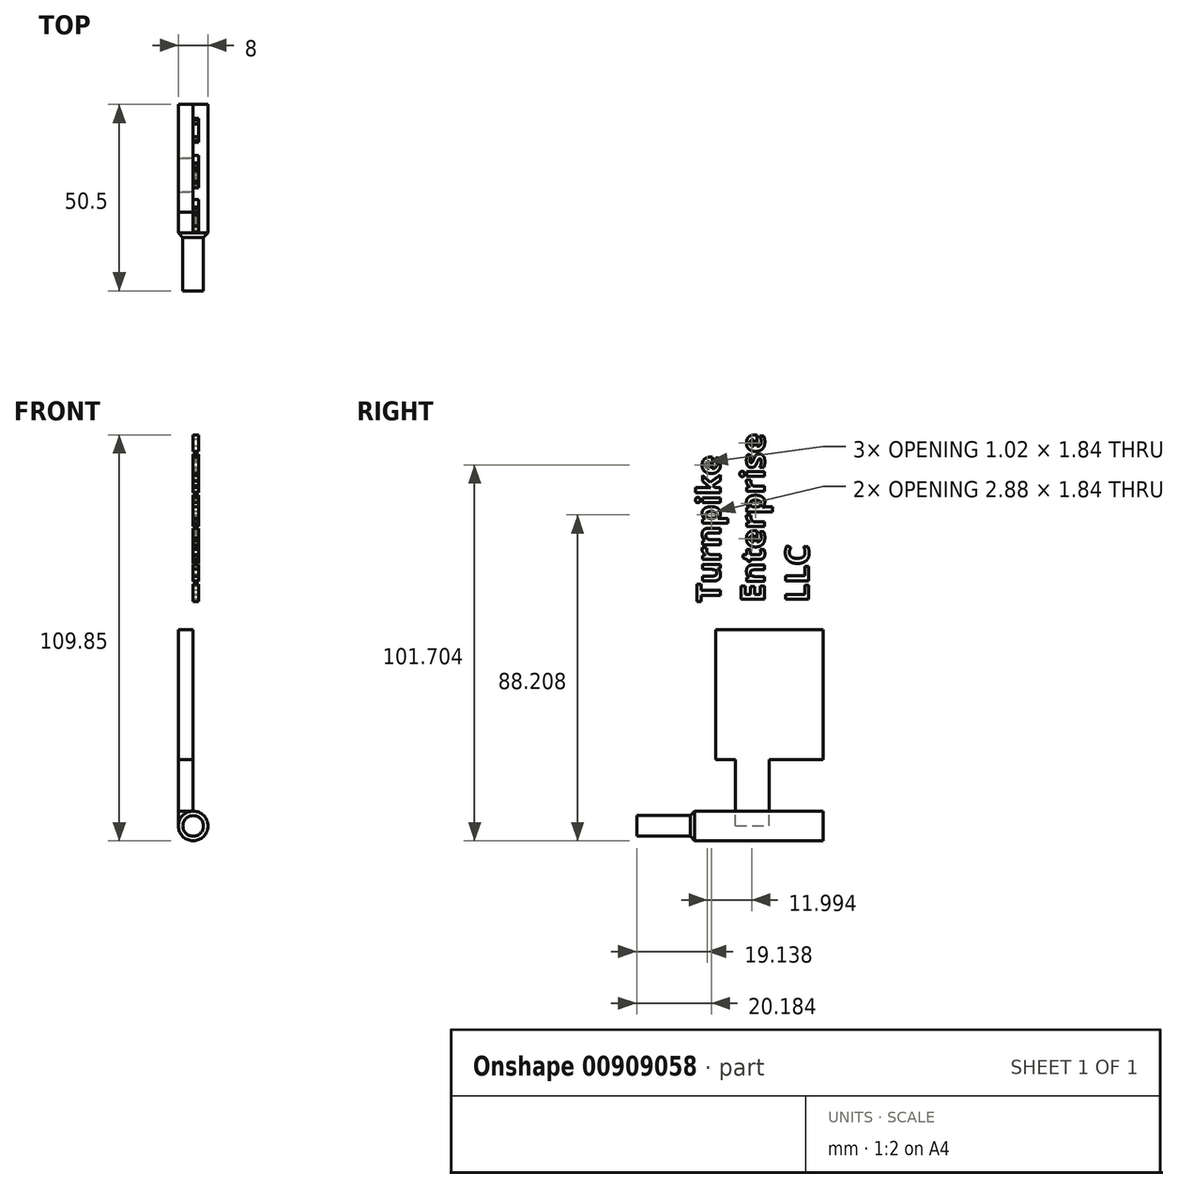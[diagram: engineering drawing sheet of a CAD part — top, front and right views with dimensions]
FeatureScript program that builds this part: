
annotation { "Feature Type Name" : "Feature", "Feature Type Description" : "" }
export const myFeature = defineFeature(function(context is Context, id is Id, definition is map)
    precondition{}
    {
        {
            var Q0;
            Q0=qCreatedBy(makeId("Right.planeOp"),FACE);
            cPlane(context, id + "F0", {"entities" : qUnion([Q0]), "cplaneType" : CPlaneType.OFFSET, "offset" : 4 * mm, "oppositeDirection" : true, "width" : 150 * mm, "height" : 150 * mm});
        }
        {
            var Q0;
            Q0=qCreatedBy(makeId("Front.planeOp"),FACE);
            var sketch = newSketch(context, id + "F1", { "sketchPlane" : qUnion([Q0])});
            skCircle(sketch, "E0", {"center": v(0, 0) * mm, "radius": 4 * mm});
            skSolve(sketch);
        }
        {
            var Q0;
            Q0=makeQuery(id+"F1.imprint","IMPRINT",FACE,{"disambiguationData":[TD([[makeQuery(id+"F1.imprint","IMPRINT",EDGE,{"derivedFrom":sQuery(id+"F1.wireOp",EDGE,"E0")}),1.0]])]});
            extrude(context, id + "F2", {"entities" : qUnion([Q0]), "endBound" : BoundingType.SYMMETRIC, "depth" : 21 * mm, "offsetDistance" : 25 * mm});
        }
        {
            var Q0;
            Q0=qCreatedBy(makeId("Front.planeOp"),FACE);
            var sketch = newSketch(context, id + "F3", { "sketchPlane" : qUnion([Q0])});
            skCircle(sketch, "E1", {"center": v(0, 0) * mm, "radius": 2.8 * mm});
            skSolve(sketch);
        }
        {
            var Q0;
            Q0 = qSketchRegion(id + "F3", true);
            extrude(context, id + "F4", {"entities" : qUnion([Q0]), "depth" : 40 * mm, "offsetDistance" : 25 * mm});
        }
        {
            var Q0;
            Q0=makeQuery(id+"F2.opExtrude","SWEPT_BODY",BODY,{"disambiguationData":[OSD([sQuery(id+"F1.wireOp",EDGE,"E0")])]});
            var Q1;
            Q1=makeQuery(id+"F4.opExtrude","SWEPT_BODY",BODY,{"disambiguationData":[OSD([sQuery(id+"F3.wireOp",EDGE,"E1")])]});
            booleanBodies(context, id + "F5", {"operationType" : BooleanOperationType.UNION, "tools" : qUnion([Q0, Q1])});
        }
        {
            var Q0;
            Q0=makeQuery(id+"F5.opBoolean","INTERSECT",EDGE,{"derivedFrom":[makeQuery(id+"F2.opExtrude","CAP_FACE",FACE,{"disambiguationData":[OSD([sQuery(id+"F1.wireOp",EDGE,"E0")])],"isStart":false}),makeQuery(id+"F4.opExtrude","SWEPT_FACE",FACE,{"disambiguationData":[OSD([sQuery(id+"F3.wireOp",EDGE,"E1")])]})]});
            chamfer(context, id + "F6", {"entities" : qUnion([Q0]), "width" : 15 * mm, "tangentPropagation" : true});
        }
        {
            var Q0;
            Q0=qCreatedBy(id+"F0.planeOp",FACE);
            var sketch = newSketch(context, id + "F7", { "sketchPlane" : qUnion([Q0])});
            skLineSegment(sketch, "E2.bottom", {"start": v(-13.27, 4) * mm, "end": v(-4.12, 4) * mm});
            skLineSegment(sketch, "E2.top", {"start": v(-13.27, 17.9) * mm, "end": v(-4.12, 17.9) * mm});
            skLineSegment(sketch, "E2.left", {"start": v(-13.27, 4) * mm, "end": v(-13.27, 17.9) * mm});
            skLineSegment(sketch, "E2.right", {"start": v(-4.12, 4) * mm, "end": v(-4.12, 17.9) * mm});
            skLineSegment(sketch, "E3", {"start": v(-26.3, 4) * mm, "end": v(-4.12, 4) * mm});
            skSolve(sketch);
        }
        {
            var Q0;
            Q0=makeQuery(id+"F7.imprint","IMPRINT",FACE,{"disambiguationData":[TD([[makeQuery(id+"F7.imprint","IMPRINT",EDGE,{"derivedFrom":sQuery(id+"F7.wireOp",EDGE,"E2.bottom")}),1.0]])]});
            extrude(context, id + "F8", {"entities" : qUnion([Q0]), "depth" : 4 * mm, "offsetDistance" : 25 * mm});
        }
        {
            var Q0;
            Q0=makeQuery(id+"F8.opExtrude","SWEPT_FACE",FACE,{"disambiguationData":[OSD([sQuery(id+"F7.wireOp",EDGE,"E2.bottom")])]});
            extrude(context, id + "F9", {"entities" : qUnion([Q0]), "endBound" : BoundingType.UP_TO_NEXT, "depth" : 25 * mm, "offsetDistance" : 25 * mm});
        }
        {
            var Q0;
            Q0=qCreatedBy(id+"F0.planeOp",FACE);
            var sketch = newSketch(context, id + "F10", { "sketchPlane" : qUnion([Q0])});
            skLineSegment(sketch, "E4.bottom", {"start": v(-18.63, 17.9) * mm, "end": v(10.5, 17.9) * mm});
            skLineSegment(sketch, "E4.top", {"start": v(-18.63, 53.17) * mm, "end": v(10.5, 53.17) * mm});
            skLineSegment(sketch, "E4.left", {"start": v(-18.63, 17.9) * mm, "end": v(-18.63, 53.17) * mm});
            skLineSegment(sketch, "E4.right", {"start": v(10.5, 17.9) * mm, "end": v(10.5, 53.17) * mm});
            skLineSegment(sketch, "E5.0", {"start": v(-13.27, 17.9) * mm, "end": v(-4.12, 17.9) * mm});
            skLineSegment(sketch, "E6.0", {"start": v(10.5, -4) * mm, "end": v(10.5, 4) * mm});
            skSolve(sketch);
        }
        {
            var Q0;
            Q0=makeQuery(id+"F10.imprint","IMPRINT",FACE,{"disambiguationData":[TD([[makeQuery(id+"F10.imprint","IMPRINT",EDGE,{"derivedFrom":sQuery(id+"F10.wireOp",EDGE,"E4.top")}),-1.0]])]});
            extrude(context, id + "F11", {"entities" : qUnion([Q0]), "operationType" : NewBodyOperationType.ADD, "depth" : 4 * mm, "offsetDistance" : 25 * mm});
        }
        {
            var Q0;
            Q0=makeQuery(id+"F11.boolean.opBoolean","MERGE",FACE,{"derivedFrom":[makeQuery(id+"F8.opExtrude","CAP_FACE",FACE,{"disambiguationData":[OSD([sQuery(id+"F7.wireOp",EDGE,"E2.bottom"),sQuery(id+"F7.wireOp",EDGE,"E2.top"),sQuery(id+"F7.wireOp",EDGE,"E2.left"),sQuery(id+"F7.wireOp",EDGE,"E2.right")])],"isStart":false}),makeQuery(id+"F11.opExtrude","CAP_FACE",FACE,{"disambiguationData":[OSD([sQuery(id+"F10.wireOp",EDGE,"E4.bottom"),sQuery(id+"F10.wireOp",EDGE,"E4.top"),sQuery(id+"F10.wireOp",EDGE,"E4.left"),sQuery(id+"F10.wireOp",EDGE,"E4.right")])],"isStart":false})]});
            var sketch = newSketch(context, id + "F12", { "sketchPlane" : qUnion([Q0])});
            skText(sketch, "E7", { "text": "Turnpike\nEnterprise\nLLC", "fontName": "OpenSans-Bold.ttf"});
            skPoint(sketch, "E7.firstSnap0", {"position": v(-15.95, 17.9) * mm});
            skPoint(sketch, "E8", {"position": v(-12.63, 20.9) * mm});
            skPoint(sketch, "E9", {"position": v(-12.63, 50.17) * mm});
            const initialGuessF12  = {"E7": [-0.0174, 0.06058, 0, 1, 0.00635]};
            skSetInitialGuess(sketch, initialGuessF12);
            skSolve(sketch);
        }
        {
            var Q0;
            Q0 = qSketchRegion(id + "F12", true);
            extrude(context, id + "F13", {"entities" : qUnion([Q0]), "operationType" : NewBodyOperationType.ADD, "depth" : 1.5 * mm, "offsetDistance" : 25 * mm});
        }
    });
